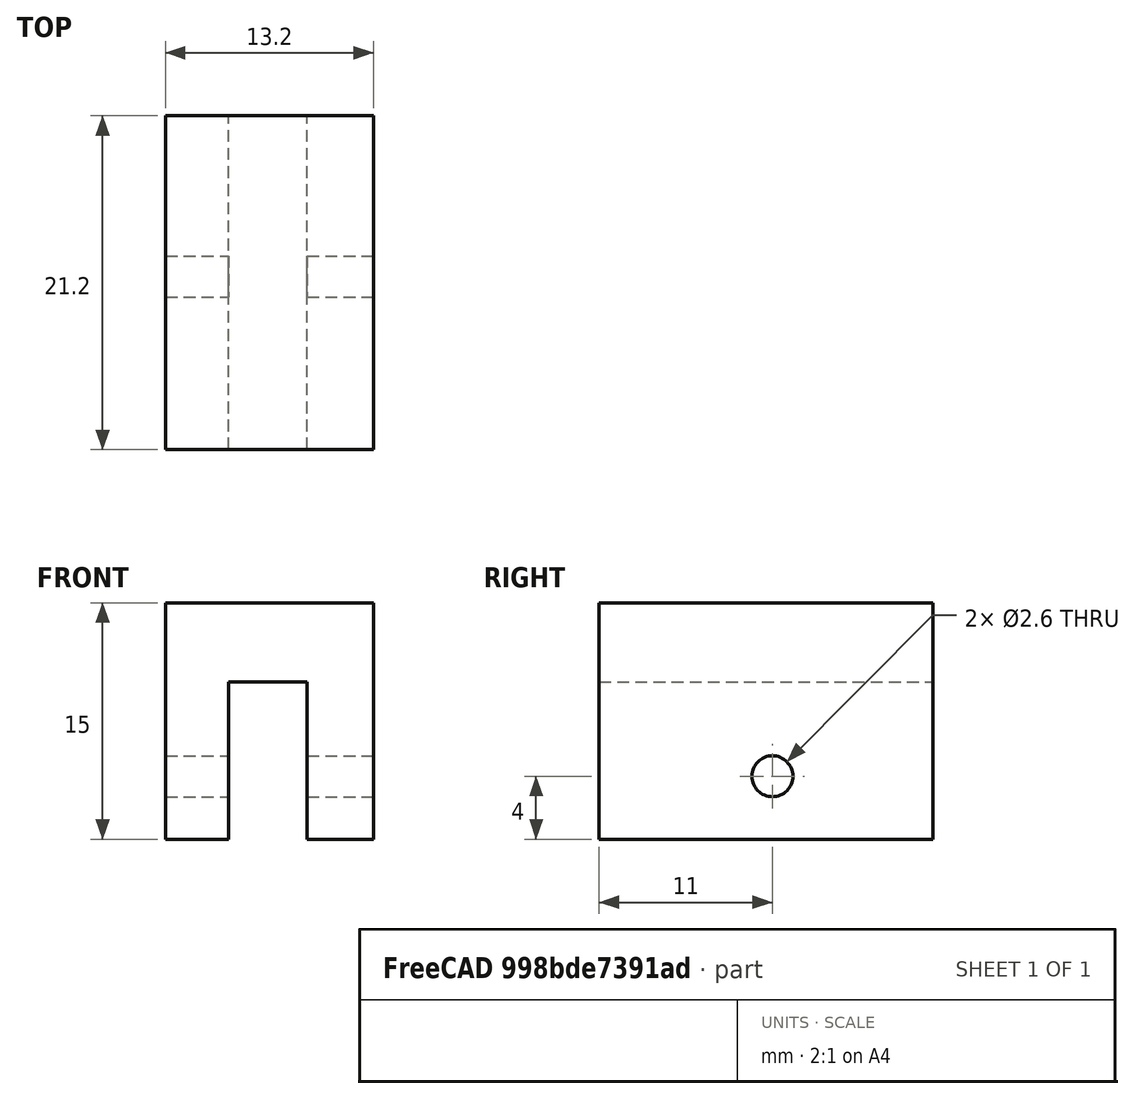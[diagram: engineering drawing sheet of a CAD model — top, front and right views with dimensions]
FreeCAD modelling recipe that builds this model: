
FCSTD DOCUMENT  (FreeCAD 0.18R16110 (Git))
Label: energy-chain-end2
License: All rights reserved
LicenseURL: http://en.wikipedia.org/wiki/All_rights_reserved
objects: Mesh::Feature×3, Part::Box×2, Part::Cut×2, Part::Cylinder×1
note: 5 computed .brp shape members not serialized (recipe doc carries the construction recipe); baked Part::Feature solids carry a one-line shape summary decoded from their .brp

FEATURE [Mesh::Feature] Difference001  label="energy-chain-end"
FEATURE [Part::Box] Box068  label="Quader047"
  AttacherType = Attacher::AttachEngine3D
  Height = 10
  Length = 5
  Placement = pos=(3.5,-1,-15) rot=(0,0,1;0rad)
  Width = 24
FEATURE [Part::Cylinder] Cylinder104  label="Zylinder092"
  Angle = 360
  AttacherType = Attacher::AttachEngine3D
  Height = 14
  Placement = pos=(-1,11,-11) rot=(0,1,0;1.5708rad)
  Radius = 1.3
FEATURE [Part::Box] Box067  label="Quader046"
  AttacherType = Attacher::AttachEngine3D
  Height = 15
  Length = 13.2
  Placement = pos=(-0.5,0,-15) rot=(0,0,1;0rad)
  Width = 21.2
FEATURE [Part::Cut] Cut119
  Base = -> Box067
  Tool = -> Cylinder104
FEATURE [Part::Cut] Cut120  label="enegy-chain-end-block"
  Base = -> Cut119
  Tool = -> Box068
FEATURE [Mesh::Feature] Mesh  label="enegy-chain-end-block(Meshed)"
FEATURE [Mesh::Feature] Mesh001  label="energy-chain-end2(Meshed)"
